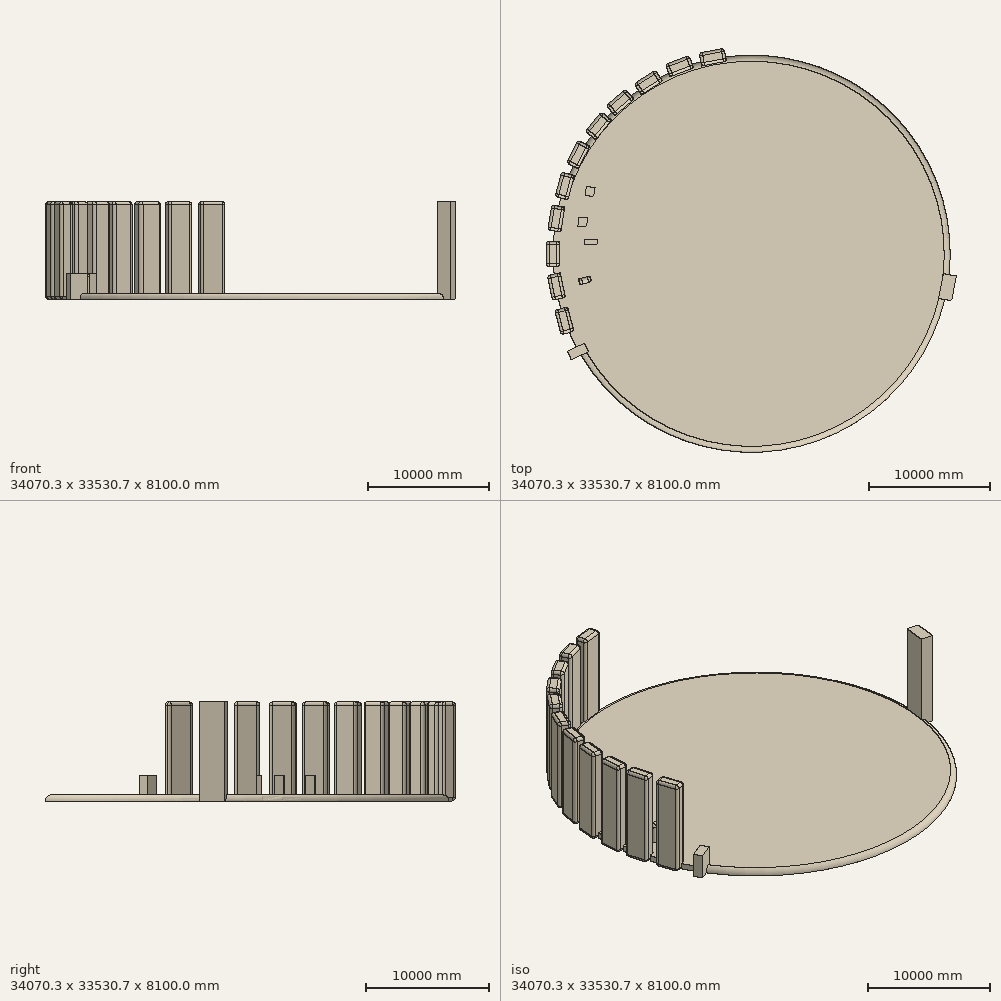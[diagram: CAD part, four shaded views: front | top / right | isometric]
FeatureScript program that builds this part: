
annotation { "Feature Type Name" : "Feature", "Feature Type Description" : "" }
export const myFeature = defineFeature(function(context is Context, id is Id, definition is map)
    precondition{}
    {
        {
            var Q0;
            Q0=qCreatedBy(makeId("Top.planeOp"),FACE);
            var sketch = newSketch(context, id + "F0", { "sketchPlane" : qUnion([Q0])});
            skCircle(sketch, "E0", {"center": v(0, 0) * mm, "radius": 16500 * mm});
            skLineSegment(sketch, "E1.bottom", {"start": v(-15950, 1050) * mm, "end": v(-17050, 1050) * mm});
            skLineSegment(sketch, "E1.top", {"start": v(-15950, -1050) * mm, "end": v(-17050, -1050) * mm});
            skLineSegment(sketch, "E1.left", {"start": v(-15950, 1050) * mm, "end": v(-15950, -1050) * mm});
            skLineSegment(sketch, "E1.right", {"start": v(-17050, 1050) * mm, "end": v(-17050, -1050) * mm});
            skPoint(sketch, "E1.middle", {"position": v(-16500, 0) * mm});
            skLineSegment(sketch, "E2.bottom", {"start": v(-15519.86, 3876.91) * mm, "end": v(-16605.6, 4053.47) * mm});
            skLineSegment(sketch, "E2.top", {"start": v(-15856.91, 1804.14) * mm, "end": v(-16942.65, 1980.7) * mm});
            skLineSegment(sketch, "E2.left", {"start": v(-15519.86, 3876.91) * mm, "end": v(-15856.91, 1804.14) * mm});
            skLineSegment(sketch, "E2.right", {"start": v(-16605.6, 4053.47) * mm, "end": v(-16942.65, 1980.7) * mm});
            skLineSegment(sketch, "E3.bottom", {"start": v(-15903.57, -1585.13) * mm, "end": v(-16980.97, -1806.97) * mm});
            skLineSegment(sketch, "E3.top", {"start": v(-15480.06, -3641.98) * mm, "end": v(-16557.46, -3863.82) * mm});
            skLineSegment(sketch, "E3.left", {"start": v(-15903.57, -1585.13) * mm, "end": v(-15480.06, -3641.98) * mm});
            skLineSegment(sketch, "E3.right", {"start": v(-16980.97, -1806.97) * mm, "end": v(-16557.46, -3863.82) * mm});
            skLineSegment(sketch, "E4.bottom", {"start": v(-15302.15, -4424.11) * mm, "end": v(-16365.17, -4706.96) * mm});
            skLineSegment(sketch, "E4.top", {"start": v(-14762.18, -6453.5) * mm, "end": v(-15825.19, -6736.35) * mm});
            skLineSegment(sketch, "E4.left", {"start": v(-15302.15, -4424.11) * mm, "end": v(-14762.18, -6453.5) * mm});
            skLineSegment(sketch, "E4.right", {"start": v(-16365.17, -4706.96) * mm, "end": v(-15825.19, -6736.35) * mm});
            skLineSegment(sketch, "E5.bottom", {"start": v(-14720.85, 6501.75) * mm, "end": v(-15783.8, 6784.83) * mm});
            skLineSegment(sketch, "E5.top", {"start": v(-15261.26, 4472.48) * mm, "end": v(-16324.22, 4755.55) * mm});
            skLineSegment(sketch, "E5.left", {"start": v(-14720.85, 6501.75) * mm, "end": v(-15261.26, 4472.48) * mm});
            skLineSegment(sketch, "E5.right", {"start": v(-15783.8, 6784.83) * mm, "end": v(-16324.22, 4755.55) * mm});
            skLineSegment(sketch, "E6.bottom", {"start": v(-13444.16, 8924.12) * mm, "end": v(-14423.41, 9425.18) * mm});
            skLineSegment(sketch, "E6.top", {"start": v(-14400.72, 7054.63) * mm, "end": v(-15379.98, 7555.69) * mm});
            skLineSegment(sketch, "E6.left", {"start": v(-13444.16, 8924.12) * mm, "end": v(-14400.72, 7054.63) * mm});
            skLineSegment(sketch, "E6.right", {"start": v(-14423.41, 9425.18) * mm, "end": v(-15379.98, 7555.69) * mm});
            skLineSegment(sketch, "E7.bottom", {"start": v(-11624.77, 11089.63) * mm, "end": v(-12476.78, 11785.4) * mm});
            skLineSegment(sketch, "E7.top", {"start": v(-12953.06, 9463.08) * mm, "end": v(-13805.06, 10158.85) * mm});
            skLineSegment(sketch, "E7.left", {"start": v(-11624.77, 11089.63) * mm, "end": v(-12953.06, 9463.08) * mm});
            skLineSegment(sketch, "E7.right", {"start": v(-12476.78, 11785.4) * mm, "end": v(-13805.06, 10158.85) * mm});
            skLineSegment(sketch, "E8.bottom", {"start": v(-9759.27, 12829.77) * mm, "end": v(-10477.5, 13662.92) * mm});
            skLineSegment(sketch, "E8.top", {"start": v(-11349.82, 11458.6) * mm, "end": v(-12068.06, 12291.74) * mm});
            skLineSegment(sketch, "E8.left", {"start": v(-9759.27, 12829.77) * mm, "end": v(-11349.82, 11458.6) * mm});
            skLineSegment(sketch, "E8.right", {"start": v(-10477.5, 13662.92) * mm, "end": v(-12068.06, 12291.74) * mm});
            skLineSegment(sketch, "E9.bottom", {"start": v(-7394.87, 14331.1) * mm, "end": v(-7993.66, 15253.83) * mm});
            skLineSegment(sketch, "E9.top", {"start": v(-9156.45, 13187.94) * mm, "end": v(-9755.25, 14110.67) * mm});
            skLineSegment(sketch, "E9.left", {"start": v(-7394.87, 14331.1) * mm, "end": v(-9156.45, 13187.94) * mm});
            skLineSegment(sketch, "E9.right", {"start": v(-7993.66, 15253.83) * mm, "end": v(-9755.25, 14110.67) * mm});
            skLineSegment(sketch, "E10.bottom", {"start": v(-4817.8, 15439.5) * mm, "end": v(-5207.76, 16468.05) * mm});
            skLineSegment(sketch, "E10.top", {"start": v(-6781.4, 14695) * mm, "end": v(-7171.37, 15723.56) * mm});
            skLineSegment(sketch, "E10.left", {"start": v(-4817.8, 15439.5) * mm, "end": v(-6781.4, 14695) * mm});
            skLineSegment(sketch, "E10.right", {"start": v(-5207.76, 16468.05) * mm, "end": v(-7171.37, 15723.56) * mm});
            skLineSegment(sketch, "E11.bottom", {"start": v(-2092.24, 15992.31) * mm, "end": v(-2297.68, 17072.96) * mm});
            skLineSegment(sketch, "E11.top", {"start": v(-4155.3, 15600.11) * mm, "end": v(-4360.73, 16680.76) * mm});
            skLineSegment(sketch, "E11.left", {"start": v(-2092.24, 15992.31) * mm, "end": v(-4155.3, 15600.11) * mm});
            skLineSegment(sketch, "E11.right", {"start": v(-2297.68, 17072.96) * mm, "end": v(-4360.73, 16680.76) * mm});
            skLineSegment(sketch, "E12.bottom", {"start": v(-13721.33, 5611.22) * mm, "end": v(-13003.34, 5484.62) * mm});
            skLineSegment(sketch, "E12.top", {"start": v(-13853.2, 4863.32) * mm, "end": v(-13135.21, 4736.72) * mm});
            skLineSegment(sketch, "E12.left", {"start": v(-13721.33, 5611.22) * mm, "end": v(-13853.2, 4863.32) * mm});
            skLineSegment(sketch, "E12.right", {"start": v(-13003.34, 5484.62) * mm, "end": v(-13135.21, 4736.72) * mm});
            skLineSegment(sketch, "E13.bottom", {"start": v(-14372.56, 3045.05) * mm, "end": v(-13645.9, 2985.8) * mm});
            skLineSegment(sketch, "E13.top", {"start": v(-14434.28, 2288.12) * mm, "end": v(-13707.62, 2228.87) * mm});
            skLineSegment(sketch, "E13.left", {"start": v(-14372.56, 3045.05) * mm, "end": v(-14434.28, 2288.12) * mm});
            skLineSegment(sketch, "E13.right", {"start": v(-13645.9, 2985.8) * mm, "end": v(-13707.62, 2228.87) * mm});
            skLineSegment(sketch, "E14.bottom", {"start": v(17020.33, -1852.2) * mm, "end": v(15940.64, -1641.82) * mm});
            skLineSegment(sketch, "E14.top", {"start": v(16618.72, -3913.43) * mm, "end": v(15539.02, -3703.06) * mm});
            skLineSegment(sketch, "E14.left", {"start": v(17020.33, -1852.2) * mm, "end": v(16618.72, -3913.43) * mm});
            skLineSegment(sketch, "E14.right", {"start": v(15940.64, -1641.82) * mm, "end": v(15539.02, -3703.06) * mm});
            skLineSegment(sketch, "E15.bottom", {"start": v(-12781.43, 1208.51) * mm, "end": v(-13891.43, 1208.51) * mm});
            skLineSegment(sketch, "E15.top", {"start": v(-12781.43, 758.51) * mm, "end": v(-13891.43, 758.51) * mm});
            skLineSegment(sketch, "E15.left", {"start": v(-12781.43, 1208.51) * mm, "end": v(-12781.43, 758.51) * mm});
            skLineSegment(sketch, "E15.right", {"start": v(-13891.43, 1208.51) * mm, "end": v(-13891.43, 758.51) * mm});
            skLineSegment(sketch, "E16.bottom", {"start": v(-14392.12, -2103.12) * mm, "end": v(-13426.2, -1844.3) * mm});
            skLineSegment(sketch, "E16.top", {"start": v(-14262.72, -2586.09) * mm, "end": v(-13296.79, -2327.27) * mm});
            skLineSegment(sketch, "E16.left", {"start": v(-14392.12, -2103.12) * mm, "end": v(-14262.72, -2586.09) * mm});
            skLineSegment(sketch, "E16.right", {"start": v(-13426.2, -1844.3) * mm, "end": v(-13296.79, -2327.27) * mm});
            skLineSegment(sketch, "E17.bottom", {"start": v(-15313.97, -8110.64) * mm, "end": v(-13891.07, -7447.13) * mm});
            skLineSegment(sketch, "E17.top", {"start": v(-14984.33, -8817.56) * mm, "end": v(-13561.43, -8154.05) * mm});
            skLineSegment(sketch, "E17.left", {"start": v(-15313.97, -8110.64) * mm, "end": v(-14984.33, -8817.56) * mm});
            skLineSegment(sketch, "E17.right", {"start": v(-13891.07, -7447.13) * mm, "end": v(-13561.43, -8154.05) * mm});
            skSolve(sketch);
        }
        {
            var Q0;
            {var subQ5=sQuery(id+"F0.wireOp",EDGE,"E4.right");Q0=makeQuery(id+"F0.imprint","IMPRINT",FACE,{"disambiguationData":[TD([[makeQuery(id+"F0.imprint","IMPRINT",EDGE,{"derivedFrom":subQ5}),1.0]])]});}
            var Q1;
            {var subQ5=sQuery(id+"F0.wireOp",EDGE,"E4.left");Q1=makeQuery(id+"F0.imprint","IMPRINT",FACE,{"disambiguationData":[TD([[makeQuery(id+"F0.imprint","IMPRINT",EDGE,{"derivedFrom":subQ5}),-1.0]])]});}
            var Q2;
            {var subQ5=sQuery(id+"F0.wireOp",EDGE,"E3.left");Q2=makeQuery(id+"F0.imprint","IMPRINT",FACE,{"disambiguationData":[TD([[makeQuery(id+"F0.imprint","IMPRINT",EDGE,{"derivedFrom":subQ5}),-1.0]])]});}
            var Q3;
            {var subQ5=sQuery(id+"F0.wireOp",EDGE,"E3.right");Q3=makeQuery(id+"F0.imprint","IMPRINT",FACE,{"disambiguationData":[TD([[makeQuery(id+"F0.imprint","IMPRINT",EDGE,{"derivedFrom":subQ5}),1.0]])]});}
            var Q4;
            {var subQ5=sQuery(id+"F0.wireOp",EDGE,"E1.right");Q4=makeQuery(id+"F0.imprint","IMPRINT",FACE,{"disambiguationData":[TD([[makeQuery(id+"F0.imprint","IMPRINT",EDGE,{"derivedFrom":subQ5}),1.0]])]});}
            var Q5;
            {var subQ5=sQuery(id+"F0.wireOp",EDGE,"E1.left");Q5=makeQuery(id+"F0.imprint","IMPRINT",FACE,{"disambiguationData":[TD([[makeQuery(id+"F0.imprint","IMPRINT",EDGE,{"derivedFrom":subQ5}),-1.0]])]});}
            var Q6;
            {var subQ5=sQuery(id+"F0.wireOp",EDGE,"E2.right");Q6=makeQuery(id+"F0.imprint","IMPRINT",FACE,{"disambiguationData":[TD([[makeQuery(id+"F0.imprint","IMPRINT",EDGE,{"derivedFrom":subQ5}),1.0]])]});}
            var Q7;
            {var subQ5=sQuery(id+"F0.wireOp",EDGE,"E2.left");Q7=makeQuery(id+"F0.imprint","IMPRINT",FACE,{"disambiguationData":[TD([[makeQuery(id+"F0.imprint","IMPRINT",EDGE,{"derivedFrom":subQ5}),-1.0]])]});}
            var Q8;
            {var subQ5=sQuery(id+"F0.wireOp",EDGE,"E14.right");Q8=makeQuery(id+"F0.imprint","IMPRINT",FACE,{"disambiguationData":[TD([[makeQuery(id+"F0.imprint","IMPRINT",EDGE,{"derivedFrom":subQ5}),1.0]])]});}
            var Q9;
            {var subQ5=sQuery(id+"F0.wireOp",EDGE,"E14.left");Q9=makeQuery(id+"F0.imprint","IMPRINT",FACE,{"disambiguationData":[TD([[makeQuery(id+"F0.imprint","IMPRINT",EDGE,{"derivedFrom":subQ5}),-1.0]])]});}
            var Q10;
            {var subQ5=sQuery(id+"F0.wireOp",EDGE,"E5.right");Q10=makeQuery(id+"F0.imprint","IMPRINT",FACE,{"disambiguationData":[TD([[makeQuery(id+"F0.imprint","IMPRINT",EDGE,{"derivedFrom":subQ5}),1.0]])]});}
            var Q11;
            {var subQ5=sQuery(id+"F0.wireOp",EDGE,"E5.left");Q11=makeQuery(id+"F0.imprint","IMPRINT",FACE,{"disambiguationData":[TD([[makeQuery(id+"F0.imprint","IMPRINT",EDGE,{"derivedFrom":subQ5}),-1.0]])]});}
            var Q12;
            {var subQ5=sQuery(id+"F0.wireOp",EDGE,"E6.right");Q12=makeQuery(id+"F0.imprint","IMPRINT",FACE,{"disambiguationData":[TD([[makeQuery(id+"F0.imprint","IMPRINT",EDGE,{"derivedFrom":subQ5}),1.0]])]});}
            var Q13;
            {var subQ5=sQuery(id+"F0.wireOp",EDGE,"E6.left");Q13=makeQuery(id+"F0.imprint","IMPRINT",FACE,{"disambiguationData":[TD([[makeQuery(id+"F0.imprint","IMPRINT",EDGE,{"derivedFrom":subQ5}),-1.0]])]});}
            var Q14;
            {var subQ5=sQuery(id+"F0.wireOp",EDGE,"E7.right");Q14=makeQuery(id+"F0.imprint","IMPRINT",FACE,{"disambiguationData":[TD([[makeQuery(id+"F0.imprint","IMPRINT",EDGE,{"derivedFrom":subQ5}),1.0]])]});}
            var Q15;
            {var subQ5=sQuery(id+"F0.wireOp",EDGE,"E7.left");Q15=makeQuery(id+"F0.imprint","IMPRINT",FACE,{"disambiguationData":[TD([[makeQuery(id+"F0.imprint","IMPRINT",EDGE,{"derivedFrom":subQ5}),-1.0]])]});}
            var Q16;
            {var subQ5=sQuery(id+"F0.wireOp",EDGE,"E8.right");Q16=makeQuery(id+"F0.imprint","IMPRINT",FACE,{"disambiguationData":[TD([[makeQuery(id+"F0.imprint","IMPRINT",EDGE,{"derivedFrom":subQ5}),1.0]])]});}
            var Q17;
            {var subQ5=sQuery(id+"F0.wireOp",EDGE,"E8.left");Q17=makeQuery(id+"F0.imprint","IMPRINT",FACE,{"disambiguationData":[TD([[makeQuery(id+"F0.imprint","IMPRINT",EDGE,{"derivedFrom":subQ5}),-1.0]])]});}
            var Q18;
            {var subQ5=sQuery(id+"F0.wireOp",EDGE,"E9.right");Q18=makeQuery(id+"F0.imprint","IMPRINT",FACE,{"disambiguationData":[TD([[makeQuery(id+"F0.imprint","IMPRINT",EDGE,{"derivedFrom":subQ5}),1.0]])]});}
            var Q19;
            {var subQ5=sQuery(id+"F0.wireOp",EDGE,"E9.left");Q19=makeQuery(id+"F0.imprint","IMPRINT",FACE,{"disambiguationData":[TD([[makeQuery(id+"F0.imprint","IMPRINT",EDGE,{"derivedFrom":subQ5}),-1.0]])]});}
            var Q20;
            {var subQ5=sQuery(id+"F0.wireOp",EDGE,"E10.right");Q20=makeQuery(id+"F0.imprint","IMPRINT",FACE,{"disambiguationData":[TD([[makeQuery(id+"F0.imprint","IMPRINT",EDGE,{"derivedFrom":subQ5}),1.0]])]});}
            var Q21;
            {var subQ5=sQuery(id+"F0.wireOp",EDGE,"E10.left");Q21=makeQuery(id+"F0.imprint","IMPRINT",FACE,{"disambiguationData":[TD([[makeQuery(id+"F0.imprint","IMPRINT",EDGE,{"derivedFrom":subQ5}),-1.0]])]});}
            var Q22;
            {var subQ5=sQuery(id+"F0.wireOp",EDGE,"E11.right");Q22=makeQuery(id+"F0.imprint","IMPRINT",FACE,{"disambiguationData":[TD([[makeQuery(id+"F0.imprint","IMPRINT",EDGE,{"derivedFrom":subQ5}),1.0]])]});}
            var Q23;
            {var subQ5=sQuery(id+"F0.wireOp",EDGE,"E11.left");Q23=makeQuery(id+"F0.imprint","IMPRINT",FACE,{"disambiguationData":[TD([[makeQuery(id+"F0.imprint","IMPRINT",EDGE,{"derivedFrom":subQ5}),-1.0]])]});}
            extrude(context, id + "F1", {"entities" : qUnion([Q0, Q1, Q2, Q3, Q4, Q5, Q6, Q7, Q8, Q9, Q10, Q11, Q12, Q13, Q14, Q15, Q16, Q17, Q18, Q19, Q20, Q21, Q22, Q23]), "depth" : 8100 * mm, "offsetDistance" : 25 * mm});
        }
        {
            var Q0;
            Q0=makeQuery(id+"F0.imprint","IMPRINT",FACE,{"disambiguationData":[TD([[makeQuery(id+"F0.imprint","IMPRINT",EDGE,{"derivedFrom":sQuery(id+"F0.wireOp",EDGE,"E12.bottom")}),-1.0]])]});
            var Q1;
            Q1=makeQuery(id+"F0.imprint","IMPRINT",FACE,{"disambiguationData":[TD([[makeQuery(id+"F0.imprint","IMPRINT",EDGE,{"derivedFrom":sQuery(id+"F0.wireOp",EDGE,"E13.bottom")}),-1.0]])]});
            var Q2;
            Q2=makeQuery(id+"F0.imprint","IMPRINT",FACE,{"disambiguationData":[TD([[makeQuery(id+"F0.imprint","IMPRINT",EDGE,{"derivedFrom":sQuery(id+"F0.wireOp",EDGE,"E15.bottom")}),1.0]])]});
            var Q3;
            Q3=makeQuery(id+"F0.imprint","IMPRINT",FACE,{"disambiguationData":[TD([[makeQuery(id+"F0.imprint","IMPRINT",EDGE,{"derivedFrom":sQuery(id+"F0.wireOp",EDGE,"E16.bottom")}),-1.0]])]});
            var Q4;
            {var subQ5=sQuery(id+"F0.wireOp",EDGE,"E17.left");Q4=makeQuery(id+"F0.imprint","IMPRINT",FACE,{"disambiguationData":[TD([[makeQuery(id+"F0.imprint","IMPRINT",EDGE,{"derivedFrom":subQ5}),1.0]])]});}
            var Q5;
            {var subQ5=sQuery(id+"F0.wireOp",EDGE,"E17.right");Q5=makeQuery(id+"F0.imprint","IMPRINT",FACE,{"disambiguationData":[TD([[makeQuery(id+"F0.imprint","IMPRINT",EDGE,{"derivedFrom":subQ5}),-1.0]])]});}
            extrude(context, id + "F2", {"entities" : qUnion([Q0, Q1, Q2, Q3, Q4, Q5]), "depth" : 2100 * mm, "offsetDistance" : 25 * mm});
        }
        {
            var Q0;
            Q0=makeQuery(id+"F1.opExtrude","CAP_EDGE",EDGE,{"disambiguationData":[OSD([sQuery(id+"F0.wireOp",EDGE,"E4.bottom")])],"isStart":false});
            var Q1;
            Q1=makeQuery(id+"F1.opExtrude","CAP_EDGE",EDGE,{"disambiguationData":[OSD([sQuery(id+"F0.wireOp",EDGE,"E4.right")])],"isStart":false});
            var Q2;
            Q2=makeQuery(id+"F1.opExtrude","CAP_EDGE",EDGE,{"disambiguationData":[OSD([sQuery(id+"F0.wireOp",EDGE,"E4.top")])],"isStart":false});
            var Q3;
            Q3=makeQuery(id+"F1.opExtrude","CAP_EDGE",EDGE,{"disambiguationData":[OSD([sQuery(id+"F0.wireOp",EDGE,"E4.left")])],"isStart":false});
            var Q4;
            Q4=makeQuery(id+"F1.opExtrude","SWEPT_EDGE",EDGE,{"disambiguationData":[OSD([sQuery(id+"F0.wireOp",EDGE,"E4.top"),sQuery(id+"F0.wireOp",EDGE,"E4.right")])]});
            var Q5;
            Q5=makeQuery(id+"F1.opExtrude","SWEPT_EDGE",EDGE,{"disambiguationData":[OSD([sQuery(id+"F0.wireOp",EDGE,"E4.bottom"),sQuery(id+"F0.wireOp",EDGE,"E4.right")])]});
            var Q6;
            Q6=makeQuery(id+"F1.opExtrude","SWEPT_EDGE",EDGE,{"disambiguationData":[OSD([sQuery(id+"F0.wireOp",EDGE,"E4.top"),sQuery(id+"F0.wireOp",EDGE,"E4.left")])]});
            var Q7;
            Q7=makeQuery(id+"F1.opExtrude","SWEPT_EDGE",EDGE,{"disambiguationData":[OSD([sQuery(id+"F0.wireOp",EDGE,"E4.bottom"),sQuery(id+"F0.wireOp",EDGE,"E4.left")])]});
            var Q8;
            Q8=makeQuery(id+"F1.opExtrude","CAP_EDGE",EDGE,{"disambiguationData":[OSD([sQuery(id+"F0.wireOp",EDGE,"E4.top")])],"isStart":true});
            var Q9;
            Q9=makeQuery(id+"F1.opExtrude","CAP_EDGE",EDGE,{"disambiguationData":[OSD([sQuery(id+"F0.wireOp",EDGE,"E4.right")])],"isStart":true});
            var Q10;
            Q10=makeQuery(id+"F1.opExtrude","CAP_EDGE",EDGE,{"disambiguationData":[OSD([sQuery(id+"F0.wireOp",EDGE,"E4.left")])],"isStart":true});
            var Q11;
            Q11=makeQuery(id+"F1.opExtrude","CAP_EDGE",EDGE,{"disambiguationData":[OSD([sQuery(id+"F0.wireOp",EDGE,"E4.bottom")])],"isStart":true});
            var Q12;
            Q12=makeQuery(id+"F1.opExtrude","CAP_EDGE",EDGE,{"disambiguationData":[OSD([sQuery(id+"F0.wireOp",EDGE,"E3.right")])],"isStart":false});
            var Q13;
            Q13=makeQuery(id+"F1.opExtrude","SWEPT_FACE",FACE,{"disambiguationData":[OSD([sQuery(id+"F0.wireOp",EDGE,"E3.right")])]});
            var Q14;
            Q14=makeQuery(id+"F1.opExtrude","SWEPT_FACE",FACE,{"disambiguationData":[OSD([sQuery(id+"F0.wireOp",EDGE,"E3.bottom")])]});
            var Q15;
            Q15=makeQuery(id+"F1.opExtrude","SWEPT_FACE",FACE,{"disambiguationData":[OSD([sQuery(id+"F0.wireOp",EDGE,"E3.left")])]});
            var Q16;
            Q16=makeQuery(id+"F1.opExtrude","SWEPT_FACE",FACE,{"disambiguationData":[OSD([sQuery(id+"F0.wireOp",EDGE,"E3.top")])]});
            var Q17;
            Q17=makeQuery(id+"F1.opExtrude","CAP_FACE",FACE,{"disambiguationData":[OSD([sQuery(id+"F0.wireOp",EDGE,"E1.bottom"),sQuery(id+"F0.wireOp",EDGE,"E1.top"),sQuery(id+"F0.wireOp",EDGE,"E1.left"),sQuery(id+"F0.wireOp",EDGE,"E1.right")])],"isStart":true});
            var Q18;
            Q18=makeQuery(id+"F1.opExtrude","CAP_FACE",FACE,{"disambiguationData":[OSD([sQuery(id+"F0.wireOp",EDGE,"E2.bottom"),sQuery(id+"F0.wireOp",EDGE,"E2.top"),sQuery(id+"F0.wireOp",EDGE,"E2.left"),sQuery(id+"F0.wireOp",EDGE,"E2.right")])],"isStart":true});
            var Q19;
            Q19=makeQuery(id+"F1.opExtrude","CAP_FACE",FACE,{"disambiguationData":[OSD([sQuery(id+"F0.wireOp",EDGE,"E5.bottom"),sQuery(id+"F0.wireOp",EDGE,"E5.top"),sQuery(id+"F0.wireOp",EDGE,"E5.left"),sQuery(id+"F0.wireOp",EDGE,"E5.right")])],"isStart":true});
            var Q20;
            Q20=makeQuery(id+"F1.opExtrude","CAP_FACE",FACE,{"disambiguationData":[OSD([sQuery(id+"F0.wireOp",EDGE,"E6.bottom"),sQuery(id+"F0.wireOp",EDGE,"E6.top"),sQuery(id+"F0.wireOp",EDGE,"E6.left"),sQuery(id+"F0.wireOp",EDGE,"E6.right")])],"isStart":true});
            var Q21;
            Q21=makeQuery(id+"F1.opExtrude","CAP_FACE",FACE,{"disambiguationData":[OSD([sQuery(id+"F0.wireOp",EDGE,"E7.bottom"),sQuery(id+"F0.wireOp",EDGE,"E7.top"),sQuery(id+"F0.wireOp",EDGE,"E7.left"),sQuery(id+"F0.wireOp",EDGE,"E7.right")])],"isStart":true});
            var Q22;
            Q22=makeQuery(id+"F1.opExtrude","CAP_EDGE",EDGE,{"disambiguationData":[OSD([sQuery(id+"F0.wireOp",EDGE,"E8.left")])],"isStart":true});
            var Q23;
            Q23=makeQuery(id+"F1.opExtrude","CAP_FACE",FACE,{"disambiguationData":[OSD([sQuery(id+"F0.wireOp",EDGE,"E9.bottom"),sQuery(id+"F0.wireOp",EDGE,"E9.top"),sQuery(id+"F0.wireOp",EDGE,"E9.left"),sQuery(id+"F0.wireOp",EDGE,"E9.right")])],"isStart":true});
            var Q24;
            Q24=makeQuery(id+"F1.opExtrude","CAP_FACE",FACE,{"disambiguationData":[OSD([sQuery(id+"F0.wireOp",EDGE,"E11.bottom"),sQuery(id+"F0.wireOp",EDGE,"E11.top"),sQuery(id+"F0.wireOp",EDGE,"E11.left"),sQuery(id+"F0.wireOp",EDGE,"E11.right")])],"isStart":true});
            var Q25;
            Q25=makeQuery(id+"F1.opExtrude","CAP_FACE",FACE,{"disambiguationData":[OSD([sQuery(id+"F0.wireOp",EDGE,"E10.bottom"),sQuery(id+"F0.wireOp",EDGE,"E10.top"),sQuery(id+"F0.wireOp",EDGE,"E10.left"),sQuery(id+"F0.wireOp",EDGE,"E10.right")])],"isStart":true});
            var Q26;
            Q26=makeQuery(id+"F1.opExtrude","CAP_FACE",FACE,{"disambiguationData":[OSD([sQuery(id+"F0.wireOp",EDGE,"E8.bottom"),sQuery(id+"F0.wireOp",EDGE,"E8.top"),sQuery(id+"F0.wireOp",EDGE,"E8.left"),sQuery(id+"F0.wireOp",EDGE,"E8.right")])],"isStart":true});
            var Q27;
            Q27=makeQuery(id+"F1.opExtrude","SWEPT_FACE",FACE,{"disambiguationData":[OSD([sQuery(id+"F0.wireOp",EDGE,"E1.right")])]});
            var Q28;
            Q28=makeQuery(id+"F1.opExtrude","SWEPT_FACE",FACE,{"disambiguationData":[OSD([sQuery(id+"F0.wireOp",EDGE,"E2.right")])]});
            var Q29;
            Q29=makeQuery(id+"F1.opExtrude","SWEPT_FACE",FACE,{"disambiguationData":[OSD([sQuery(id+"F0.wireOp",EDGE,"E5.right")])]});
            var Q30;
            Q30=makeQuery(id+"F1.opExtrude","SWEPT_FACE",FACE,{"disambiguationData":[OSD([sQuery(id+"F0.wireOp",EDGE,"E6.right")])]});
            var Q31;
            Q31=makeQuery(id+"F1.opExtrude","SWEPT_FACE",FACE,{"disambiguationData":[OSD([sQuery(id+"F0.wireOp",EDGE,"E7.right")])]});
            var Q32;
            Q32=makeQuery(id+"F1.opExtrude","SWEPT_FACE",FACE,{"disambiguationData":[OSD([sQuery(id+"F0.wireOp",EDGE,"E8.right")])]});
            var Q33;
            Q33=makeQuery(id+"F1.opExtrude","SWEPT_EDGE",EDGE,{"disambiguationData":[OSD([sQuery(id+"F0.wireOp",EDGE,"E9.bottom"),sQuery(id+"F0.wireOp",EDGE,"E9.right")])]});
            var Q34;
            Q34=makeQuery(id+"F1.opExtrude","SWEPT_FACE",FACE,{"disambiguationData":[OSD([sQuery(id+"F0.wireOp",EDGE,"E9.right")])]});
            var Q35;
            Q35=makeQuery(id+"F1.opExtrude","SWEPT_FACE",FACE,{"disambiguationData":[OSD([sQuery(id+"F0.wireOp",EDGE,"E10.right")])]});
            var Q36;
            Q36=makeQuery(id+"F1.opExtrude","SWEPT_FACE",FACE,{"disambiguationData":[OSD([sQuery(id+"F0.wireOp",EDGE,"E11.right")])]});
            var Q37;
            Q37=makeQuery(id+"F1.opExtrude","CAP_FACE",FACE,{"disambiguationData":[OSD([sQuery(id+"F0.wireOp",EDGE,"E1.bottom"),sQuery(id+"F0.wireOp",EDGE,"E1.top"),sQuery(id+"F0.wireOp",EDGE,"E1.left"),sQuery(id+"F0.wireOp",EDGE,"E1.right")])],"isStart":false});
            var Q38;
            Q38=makeQuery(id+"F1.opExtrude","CAP_FACE",FACE,{"disambiguationData":[OSD([sQuery(id+"F0.wireOp",EDGE,"E2.bottom"),sQuery(id+"F0.wireOp",EDGE,"E2.top"),sQuery(id+"F0.wireOp",EDGE,"E2.left"),sQuery(id+"F0.wireOp",EDGE,"E2.right")])],"isStart":false});
            var Q39;
            Q39=makeQuery(id+"F1.opExtrude","CAP_FACE",FACE,{"disambiguationData":[OSD([sQuery(id+"F0.wireOp",EDGE,"E5.bottom"),sQuery(id+"F0.wireOp",EDGE,"E5.top"),sQuery(id+"F0.wireOp",EDGE,"E5.left"),sQuery(id+"F0.wireOp",EDGE,"E5.right")])],"isStart":false});
            var Q40;
            Q40=makeQuery(id+"F1.opExtrude","CAP_FACE",FACE,{"disambiguationData":[OSD([sQuery(id+"F0.wireOp",EDGE,"E6.bottom"),sQuery(id+"F0.wireOp",EDGE,"E6.top"),sQuery(id+"F0.wireOp",EDGE,"E6.left"),sQuery(id+"F0.wireOp",EDGE,"E6.right")])],"isStart":false});
            var Q41;
            Q41=makeQuery(id+"F1.opExtrude","CAP_FACE",FACE,{"disambiguationData":[OSD([sQuery(id+"F0.wireOp",EDGE,"E7.bottom"),sQuery(id+"F0.wireOp",EDGE,"E7.top"),sQuery(id+"F0.wireOp",EDGE,"E7.left"),sQuery(id+"F0.wireOp",EDGE,"E7.right")])],"isStart":false});
            var Q42;
            Q42=makeQuery(id+"F1.opExtrude","CAP_FACE",FACE,{"disambiguationData":[OSD([sQuery(id+"F0.wireOp",EDGE,"E8.bottom"),sQuery(id+"F0.wireOp",EDGE,"E8.top"),sQuery(id+"F0.wireOp",EDGE,"E8.left"),sQuery(id+"F0.wireOp",EDGE,"E8.right")])],"isStart":false});
            var Q43;
            Q43=makeQuery(id+"F1.opExtrude","CAP_EDGE",EDGE,{"disambiguationData":[OSD([sQuery(id+"F0.wireOp",EDGE,"E9.left")])],"isStart":false});
            var Q44;
            Q44=makeQuery(id+"F1.opExtrude","CAP_EDGE",EDGE,{"disambiguationData":[OSD([sQuery(id+"F0.wireOp",EDGE,"E10.left")])],"isStart":false});
            var Q45;
            Q45=makeQuery(id+"F1.opExtrude","CAP_FACE",FACE,{"disambiguationData":[OSD([sQuery(id+"F0.wireOp",EDGE,"E11.bottom"),sQuery(id+"F0.wireOp",EDGE,"E11.top"),sQuery(id+"F0.wireOp",EDGE,"E11.left"),sQuery(id+"F0.wireOp",EDGE,"E11.right")])],"isStart":false});
            var Q46;
            Q46=makeQuery(id+"F1.opExtrude","SWEPT_FACE",FACE,{"disambiguationData":[OSD([sQuery(id+"F0.wireOp",EDGE,"E1.left")])]});
            var Q47;
            Q47=makeQuery(id+"F1.opExtrude","SWEPT_FACE",FACE,{"disambiguationData":[OSD([sQuery(id+"F0.wireOp",EDGE,"E2.left")])]});
            var Q48;
            Q48=makeQuery(id+"F1.opExtrude","SWEPT_FACE",FACE,{"disambiguationData":[OSD([sQuery(id+"F0.wireOp",EDGE,"E5.left")])]});
            var Q49;
            Q49=makeQuery(id+"F1.opExtrude","SWEPT_FACE",FACE,{"disambiguationData":[OSD([sQuery(id+"F0.wireOp",EDGE,"E6.left")])]});
            var Q50;
            Q50=makeQuery(id+"F1.opExtrude","SWEPT_FACE",FACE,{"disambiguationData":[OSD([sQuery(id+"F0.wireOp",EDGE,"E7.left")])]});
            var Q51;
            Q51=makeQuery(id+"F1.opExtrude","SWEPT_FACE",FACE,{"disambiguationData":[OSD([sQuery(id+"F0.wireOp",EDGE,"E8.left")])]});
            var Q52;
            Q52=makeQuery(id+"F1.opExtrude","SWEPT_FACE",FACE,{"disambiguationData":[OSD([sQuery(id+"F0.wireOp",EDGE,"E9.left")])]});
            var Q53;
            Q53=makeQuery(id+"F1.opExtrude","SWEPT_FACE",FACE,{"disambiguationData":[OSD([sQuery(id+"F0.wireOp",EDGE,"E11.left")])]});
            var Q54;
            Q54=makeQuery(id+"F1.opExtrude","SWEPT_EDGE",EDGE,{"disambiguationData":[OSD([sQuery(id+"F0.wireOp",EDGE,"E10.bottom"),sQuery(id+"F0.wireOp",EDGE,"E10.left")])]});
            var Q55;
            Q55=makeQuery(id+"F1.opExtrude","CAP_EDGE",EDGE,{"disambiguationData":[OSD([sQuery(id+"F0.wireOp",EDGE,"E10.bottom")])],"isStart":false});
            var Q56;
            Q56=makeQuery(id+"F1.opExtrude","SWEPT_FACE",FACE,{"disambiguationData":[OSD([sQuery(id+"F0.wireOp",EDGE,"E9.bottom")])]});
            var Q57;
            Q57=makeQuery(id+"F1.opExtrude","SWEPT_FACE",FACE,{"disambiguationData":[OSD([sQuery(id+"F0.wireOp",EDGE,"E10.top")])]});
            var Q58;
            Q58=makeQuery(id+"F1.opExtrude","SWEPT_FACE",FACE,{"disambiguationData":[OSD([sQuery(id+"F0.wireOp",EDGE,"E9.top")])]});
            var Q59;
            Q59=makeQuery(id+"F2.opExtrude","SWEPT_FACE",FACE,{"disambiguationData":[OSD([sQuery(id+"F0.wireOp",EDGE,"E16.top")])]});
            var Q60;
            Q60=makeQuery(id+"F2.opExtrude","SWEPT_EDGE",EDGE,{"disambiguationData":[OSD([sQuery(id+"F0.wireOp",EDGE,"E16.top"),sQuery(id+"F0.wireOp",EDGE,"E16.right")])]});
            var Q61;
            Q61=makeQuery(id+"F2.opExtrude","CAP_FACE",FACE,{"disambiguationData":[OSD([sQuery(id+"F0.wireOp",EDGE,"E16.bottom"),sQuery(id+"F0.wireOp",EDGE,"E16.top"),sQuery(id+"F0.wireOp",EDGE,"E16.left"),sQuery(id+"F0.wireOp",EDGE,"E16.right")])],"isStart":false});
            var Q62;
            Q62=makeQuery(id+"F2.opExtrude","SWEPT_EDGE",EDGE,{"disambiguationData":[OSD([sQuery(id+"F0.wireOp",EDGE,"E16.bottom"),sQuery(id+"F0.wireOp",EDGE,"E16.right")])]});
            var Q63;
            Q63=makeQuery(id+"F2.opExtrude","SWEPT_FACE",FACE,{"disambiguationData":[OSD([sQuery(id+"F0.wireOp",EDGE,"E16.bottom")])]});
            var Q64;
            Q64=makeQuery(id+"F2.opExtrude","CAP_EDGE",EDGE,{"disambiguationData":[OSD([sQuery(id+"F0.wireOp",EDGE,"E16.right")])],"isStart":true});
            var Q65;
            Q65=makeQuery(id+"F2.opExtrude","CAP_EDGE",EDGE,{"disambiguationData":[OSD([sQuery(id+"F0.wireOp",EDGE,"E16.left")])],"isStart":true});
            fillet(context, id + "F3", {"entities" : qUnion([Q0, Q1, Q2, Q3, Q4, Q5, Q6, Q7, Q8, Q9, Q10, Q11, Q12, Q13, Q14, Q15, Q16, Q17, Q18, Q19, Q20, Q21, Q22, Q23, Q24, Q25, Q26, Q27, Q28, Q29, Q30, Q31, Q32, Q33, Q34, Q35, Q36, Q37, Q38, Q39, Q40, Q41, Q42, Q43, Q44, Q45, Q46, Q47, Q48, Q49, Q50, Q51, Q52, Q53, Q54, Q55, Q56, Q57, Q58, Q59, Q60, Q61, Q62, Q63, Q64, Q65]), "radius" : 250 * mm, "tangentPropagation" : true, "allowEdgeOverflow" : false});
        }
        {
            var Q0;
            {var subQ50=sQuery(id+"F0.wireOp",EDGE,"E1.left");Q0=makeQuery(id+"F0.imprint","IMPRINT",FACE,{"disambiguationData":[TD([[makeQuery(id+"F0.imprint","IMPRINT",EDGE,{"derivedFrom":subQ50}),1.0]])]});}
            extrude(context, id + "F4", {"entities" : qUnion([Q0]), "depth" : 500 * mm, "offsetDistance" : 25 * mm});
        }
        {
            var Q0;
            {var subQ0=sQuery(id+"F0.wireOp",EDGE,"E0");Q0=makeQuery(id+"F4.opExtrude","CAP_EDGE",EDGE,{"disambiguationData":[OSD([subQ0]),TDD([makeQuery(id+"F0.imprint","IMPRINT",EDGE,{"disambiguationData":[TD([[makeQuery(id+"F0.imprint","INTERSECT",VERTEX,{"derivedFrom":[subQ0,sQuery(id+"F0.wireOp",EDGE,"E17.top")]}),-1.0]])],"derivedFrom":subQ0})])],"isStart":false});}
            var Q1;
            {var subQ0=sQuery(id+"F0.wireOp",EDGE,"E0");Q1=makeQuery(id+"F4.opExtrude","CAP_EDGE",EDGE,{"disambiguationData":[OSD([subQ0]),TDD([makeQuery(id+"F0.imprint","IMPRINT",EDGE,{"disambiguationData":[TD([[makeQuery(id+"F0.imprint","INTERSECT",VERTEX,{"derivedFrom":[subQ0,sQuery(id+"F0.wireOp",EDGE,"E11.bottom")]}),1.0]])],"derivedFrom":subQ0})])],"isStart":false});}
            fillet(context, id + "F5", {"entities" : qUnion([Q0, Q1]), "radius" : 500 * mm, "tangentPropagation" : true, "allowEdgeOverflow" : false});
        }
    });
